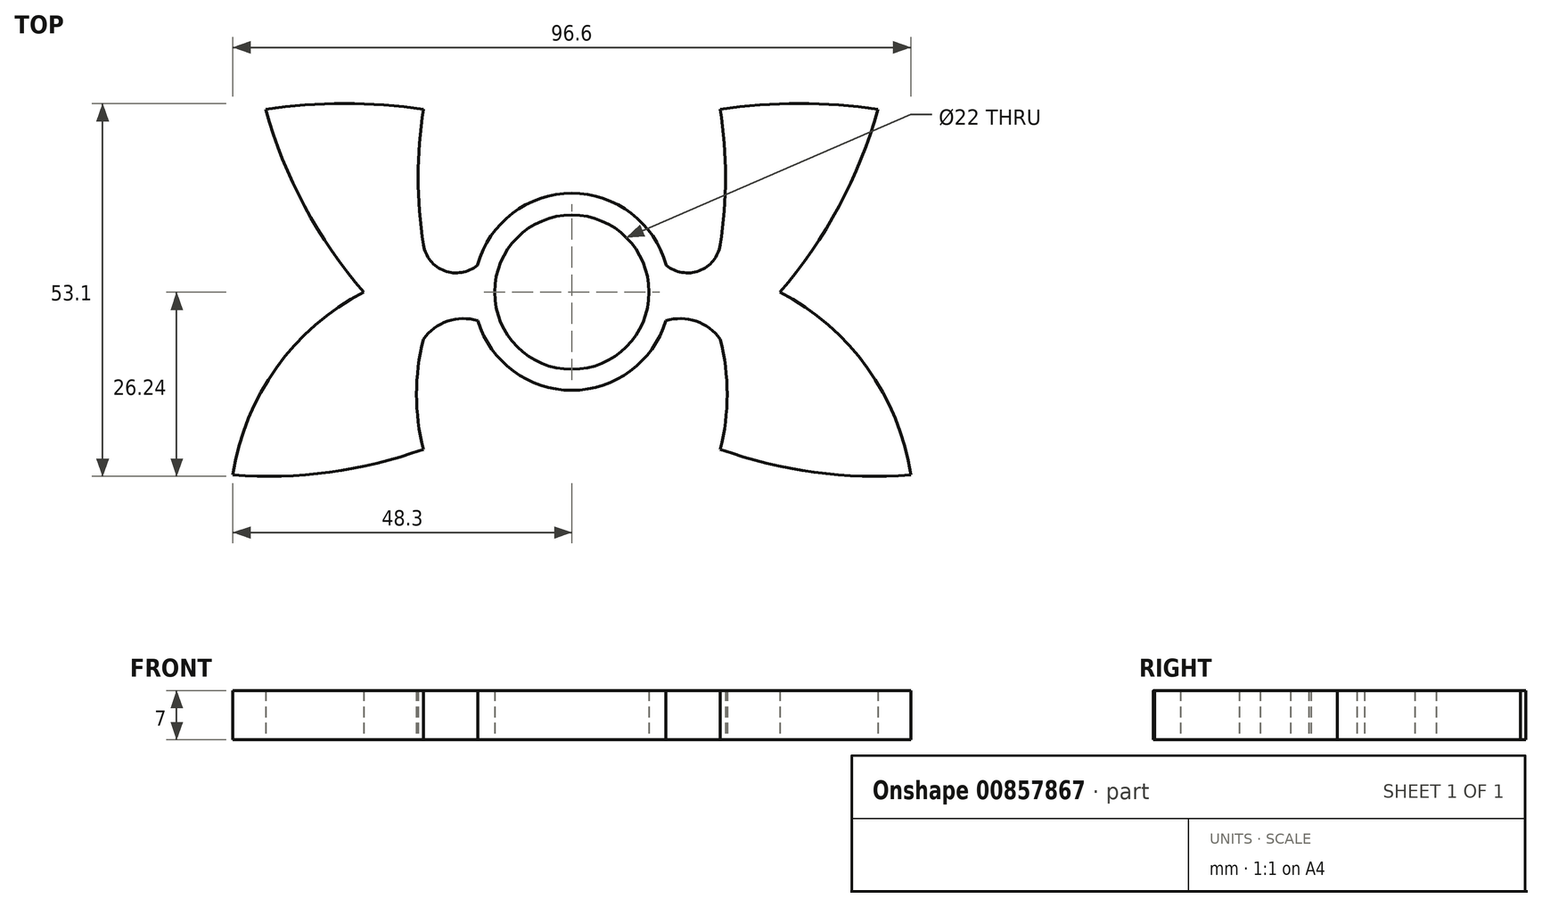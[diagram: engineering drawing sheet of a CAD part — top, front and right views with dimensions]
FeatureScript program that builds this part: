
annotation { "Feature Type Name" : "Feature", "Feature Type Description" : "" }
export const myFeature = defineFeature(function(context is Context, id is Id, definition is map)
    precondition{}
    {
        {
            var Q0;
            Q0=qCreatedBy(makeId("Top.planeOp"),FACE);
            var sketch = newSketch(context, id + "F0", { "sketchPlane" : qUnion([Q0])});
            skCircle(sketch, "E0", {"center": v(0, 0) * mm, "radius": 11 * mm});
            skArc(sketch, "E1", {"start": v(-21.15, 6.73) * mm, "mid": v(-18.15, 3.05) * mm, "end": v(-13.46, 3.83) * mm});
            skArc(sketch, "E2", {"start": v(-21.15, 26.05) * mm, "mid": v(-21.9, 16.39) * mm, "end": v(-21.15, 6.73) * mm});
            skArc(sketch, "E3", {"start": v(-21.15, 26.05) * mm, "mid": v(-32.4, 26.86) * mm, "end": v(-43.65, 26.05) * mm});
            skArc(sketch, "E4", {"start": v(-43.65, 26.05) * mm, "mid": v(-38.08, 12.25) * mm, "end": v(-29.64, 0) * mm});
            skArc(sketch, "E5", {"start": v(-29.64, 0) * mm, "mid": v(-42.11, -10.77) * mm, "end": v(-48.3, -26.05) * mm});
            skArc(sketch, "E6", {"start": v(-48.3, -26.05) * mm, "mid": v(-34.53, -25.65) * mm, "end": v(-21.15, -22.38) * mm});
            skArc(sketch, "E7", {"start": v(-21.15, -6.73) * mm, "mid": v(-22.13, -14.55) * mm, "end": v(-21.15, -22.38) * mm});
            skArc(sketch, "E8", {"start": v(-13.4, -4.08) * mm, "mid": v(-17.7, -4.14) * mm, "end": v(-21.15, -6.73) * mm});
            skLineSegment(sketch, "E9.direction1", {"start": v(-29.64, 0) * mm, "end": v(-4.64, 0) * mm, "construction": true});
            skArc(sketch, "E10.MirrorCS", {"start": v(21.15, 26.05) * mm, "mid": v(21.9, 16.39) * mm, "end": v(21.15, 6.73) * mm});
            skArc(sketch, "E11.MirrorCS", {"start": v(21.15, 6.73) * mm, "mid": v(18.15, 3.05) * mm, "end": v(13.46, 3.83) * mm});
            skArc(sketch, "E12.MirrorCS", {"start": v(21.15, 26.05) * mm, "mid": v(32.4, 26.86) * mm, "end": v(43.65, 26.05) * mm});
            skArc(sketch, "E13.MirrorCS", {"start": v(43.65, 26.05) * mm, "mid": v(38.08, 12.25) * mm, "end": v(29.64, 0) * mm});
            skArc(sketch, "E14.MirrorCS", {"start": v(29.64, 0) * mm, "mid": v(42.11, -10.77) * mm, "end": v(48.3, -26.05) * mm});
            skArc(sketch, "E15.MirrorCS", {"start": v(48.3, -26.05) * mm, "mid": v(34.53, -25.65) * mm, "end": v(21.15, -22.38) * mm});
            skArc(sketch, "E16.MirrorCS", {"start": v(21.15, -6.73) * mm, "mid": v(22.13, -14.55) * mm, "end": v(21.15, -22.38) * mm});
            skArc(sketch, "E17.MirrorCS", {"start": v(13.4, -4.08) * mm, "mid": v(17.7, -4.14) * mm, "end": v(21.15, -6.73) * mm});
            skArc(sketch, "E18", {"start": v(13.46, 3.83) * mm, "mid": v(0, 14.08) * mm, "end": v(-13.46, 3.83) * mm});
            skArc(sketch, "E19", {"start": v(-13.4, -4.08) * mm, "mid": v(0, -13.99) * mm, "end": v(13.4, -4.08) * mm});
            skSolve(sketch);
        }
        {
            var Q0;
            Q0=makeQuery(id+"F0.imprint","IMPRINT",FACE,{"disambiguationData":[TD([[makeQuery(id+"F0.imprint","IMPRINT",EDGE,{"derivedFrom":sQuery(id+"F0.wireOp",EDGE,"E0")}),-1.0]])]});
            extrude(context, id + "F1", {"entities" : qUnion([Q0]), "depth" : 7 * mm, "offsetDistance" : 25 * mm});
        }
    });
